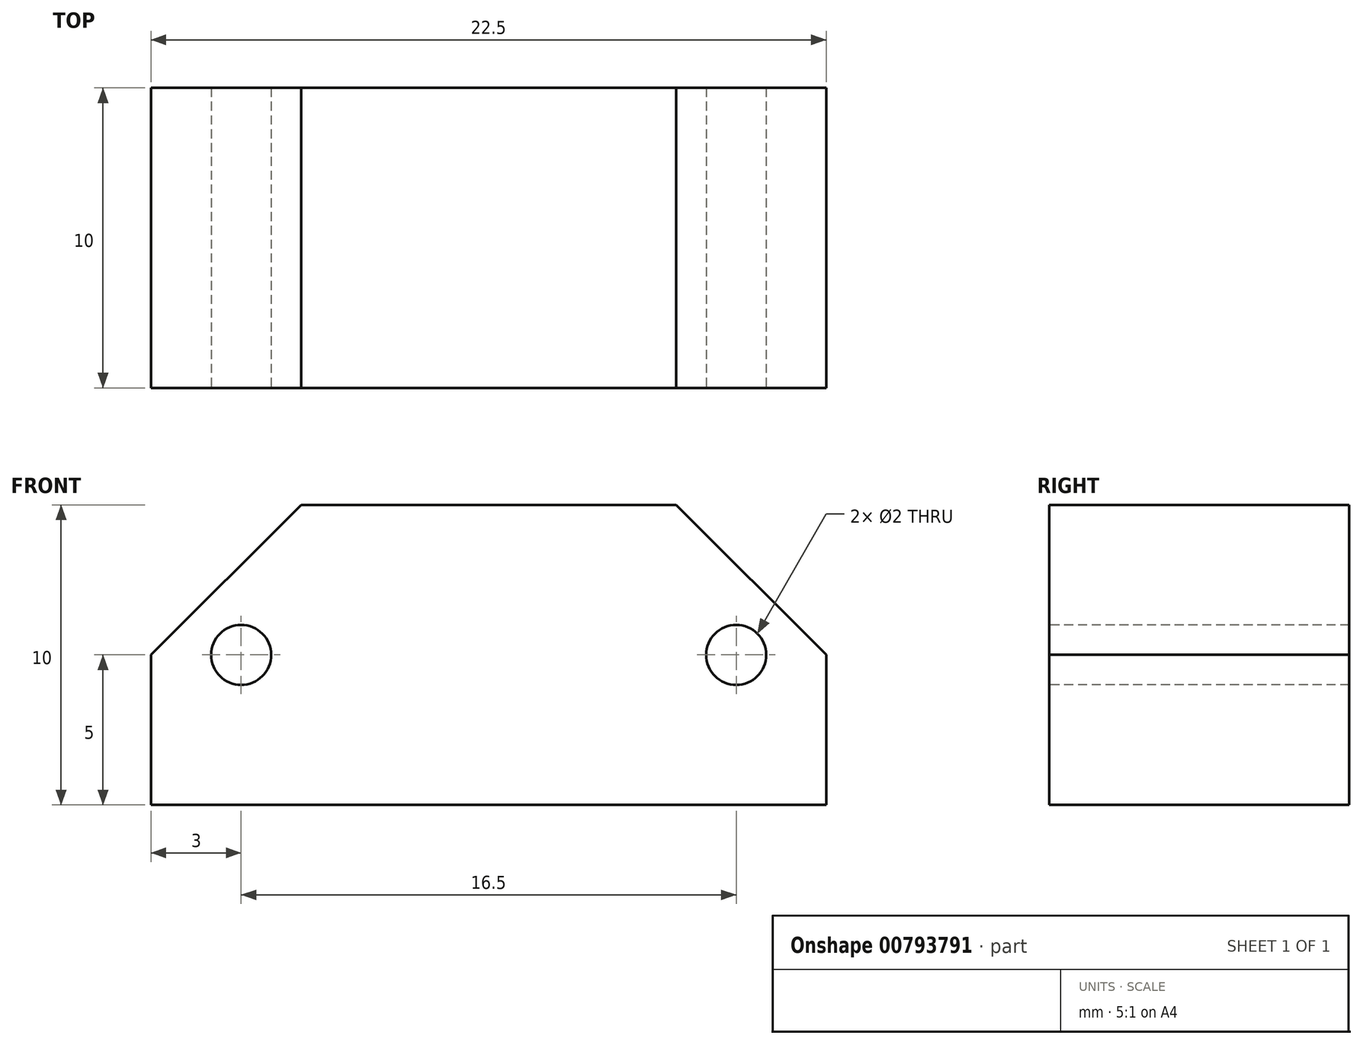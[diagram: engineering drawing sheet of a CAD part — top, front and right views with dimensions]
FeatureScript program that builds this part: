
annotation { "Feature Type Name" : "Feature", "Feature Type Description" : "" }
export const myFeature = defineFeature(function(context is Context, id is Id, definition is map)
    precondition{}
    {
        {
            var Q0;
            Q0=qCreatedBy(makeId("Top.planeOp"),FACE);
            var sketch = newSketch(context, id + "F0", { "sketchPlane" : qUnion([Q0])});
            skLineSegment(sketch, "E0.bottom", {"start": v(11.25, -5) * mm, "end": v(-11.25, -5) * mm});
            skLineSegment(sketch, "E0.top", {"start": v(11.25, 5) * mm, "end": v(-11.25, 5) * mm});
            skLineSegment(sketch, "E0.left", {"start": v(11.25, -5) * mm, "end": v(11.25, 5) * mm});
            skLineSegment(sketch, "E0.right", {"start": v(-11.25, -5) * mm, "end": v(-11.25, 5) * mm});
            skPoint(sketch, "E0.middle", {"position": v(0, 0) * mm});
            skSolve(sketch);
        }
        {
            var Q0;
            Q0=makeQuery(id+"F0.imprint","IMPRINT",FACE,{"disambiguationData":[TD([[makeQuery(id+"F0.imprint","IMPRINT",EDGE,{"derivedFrom":sQuery(id+"F0.wireOp",EDGE,"E0.bottom")}),-1.0]])]});
            extrude(context, id + "F1", {"entities" : qUnion([Q0]), "depth" : 10 * mm, "offsetDistance" : 25 * mm});
        }
        {
            var Q0;
            Q0=makeQuery(id+"F1.opExtrude","SWEPT_FACE",FACE,{"disambiguationData":[OSD([sQuery(id+"F0.wireOp",EDGE,"E0.bottom")])]});
            var sketch = newSketch(context, id + "F2", { "sketchPlane" : qUnion([Q0])});
            skLineSegment(sketch, "E1", {"start": v(-11.25, 0) * mm, "end": v(-8.25, 0) * mm});
            skLineSegment(sketch, "E2", {"start": v(-8.25, 0) * mm, "end": v(-8.25, 5) * mm});
            skLineSegment(sketch, "E3", {"start": v(11.25, 0) * mm, "end": v(8.25, 0) * mm});
            skLineSegment(sketch, "E4", {"start": v(8.25, 0) * mm, "end": v(8.25, 5) * mm});
            skCircle(sketch, "E5", {"center": v(-8.25, 5) * mm, "radius": 1 * mm});
            skCircle(sketch, "E6", {"center": v(8.25, 5) * mm, "radius": 1 * mm});
            skSolve(sketch);
        }
        {
            var Q0;
            Q0=makeQuery(id+"F2.imprint","IMPRINT",FACE,{"disambiguationData":[TD([[makeQuery(id+"F2.imprint","IMPRINT",EDGE,{"derivedFrom":sQuery(id+"F2.wireOp",EDGE,"E5")}),1.0]])]});
            var Q1;
            Q1=makeQuery(id+"F2.imprint","IMPRINT",FACE,{"disambiguationData":[TD([[makeQuery(id+"F2.imprint","IMPRINT",EDGE,{"derivedFrom":sQuery(id+"F2.wireOp",EDGE,"E6")}),1.0]])]});
            extrude(context, id + "F3", {"entities" : qUnion([Q0, Q1]), "operationType" : NewBodyOperationType.REMOVE, "oppositeDirection" : true, "depth" : 25 * mm, "offsetDistance" : 25 * mm});
        }
        {
            var Q0;
            Q0=makeQuery(id+"F1.opExtrude","CAP_EDGE",EDGE,{"disambiguationData":[OSD([sQuery(id+"F0.wireOp",EDGE,"E0.right")])],"isStart":false});
            var Q1;
            Q1=makeQuery(id+"F1.opExtrude","CAP_EDGE",EDGE,{"disambiguationData":[OSD([sQuery(id+"F0.wireOp",EDGE,"E0.left")])],"isStart":false});
            chamfer(context, id + "F4", {"entities" : qUnion([Q0, Q1]), "width" : 5 * mm, "tangentPropagation" : true});
        }
    });
